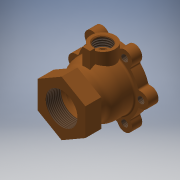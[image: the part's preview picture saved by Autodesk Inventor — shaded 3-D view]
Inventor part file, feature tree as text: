
AUTODESK INVENTOR PART (.ipt)
format: ipt  version: 2018 (Build 220112000, 112)  size: 359,424 bytes
history: native  units: mm (DEFAULTED — no unit token found)
features: sketch x7, extrude x4, fillet x2, hole x2, thread x2, plane x2, revolve x1, pattern_circular x1, chamfer x1
ambient origin geometry x8: Origin, YZ Plane, XZ Plane, XY Plane, X Axis, Y Axis, Z Axis, Center Point
bodies: Solid1 (feature_tree)
feature tree (22):
  revolve  "Revolution1"  [1 undecoded]
  extrude  "Extrusion1"  Depth=46.0mm
  extrude  "Extrusion2"  Depth=63.0mm
  fillet  "Fillet1"  Radius=74.0mm
  hole  "Hole1"  [1 undecoded]
  pattern_circular  "Circular Pattern1"  [2 undecoded]
  thread  "Thread1"  [1 undecoded]
  fillet  "Fillet2"  Radius=22.0mm
  plane  "Work Plane1"
  extrude  "Extrusion3"  Depth=9.0mm
  hole  "Hole4"  [1 undecoded]
  chamfer  "Chamfer2"  Distance=57.0mm
  thread  "Thread3"  [1 undecoded]
  plane  "Work Plane3"
  extrude  "Extrusion5"  Depth=9.0mm
  sketch  "Sketch1"  dims[d0=54.0mm d1=38.0mm]
  sketch  "Sketch2"  dims[d2=32.0mm d3=46.0mm]
  sketch  "Sketch3"  dims[d4=57.0mm d5=63.0mm d6=74.0mm]
  sketch  "Sketch4"  dims[d7=12.0mm d8=68.0mm]
  sketch  "Sketch5"  dims[d9=26.0mm]
  sketch  "Sketch6"  dims[d10=18.0mm]
  sketch  "Sketch8"  dims[d11=21.0mm d12=24.0mm d13=33.0mm d14=22.0mm d15=10.0mm d16=90.0deg d17=57.0mm d18=19.0mm d19=0.0mm d20=78.0mm d21=9.0mm d22=12.0mm d23=0.0mm d24=2.0mm d25=8.0mm d26=6.0mm d27=4.0mm d28=2.0mm d29=14.3117mm d30=8.0mm d31=20.594885mm d32=60.0mm d34=360.0deg d35=10.0mm d36=0.0mm d37=2.0mm d38=44.0mm d39=29.0mm d40=18.5mm d41=12.0mm d42=0.0mm d68=16.0mm d69=6.0mm d70=20.0mm d71=12.0mm d72=14.3117mm d73=8.0mm d74=20.594885mm d75=1.0mm d76=45.0deg d77=10.0mm d78=0.0mm d79=47.0mm d80=32.5mm d81=6.0mm d82=4.5mm d83=9.0mm d84=10.0mm d85=0.0mm d86=1.0mm]
note: 7 required parameter values undecoded (feature->parameter linkage not recoverable at this tier; creation-order binding heuristic only, values carry confidence <= 0.55)